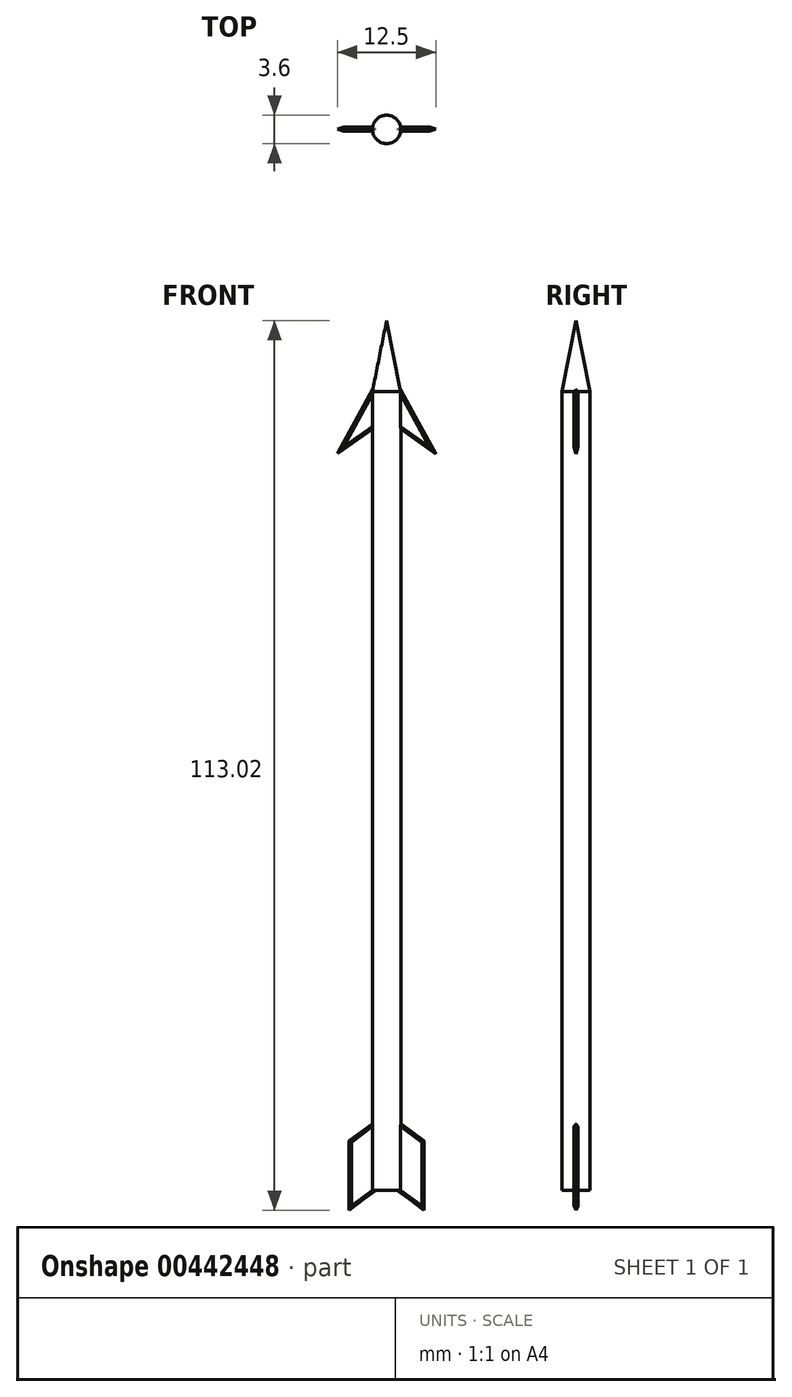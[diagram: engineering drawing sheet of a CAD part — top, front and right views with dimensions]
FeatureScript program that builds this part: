
annotation { "Feature Type Name" : "Feature", "Feature Type Description" : "" }
export const myFeature = defineFeature(function(context is Context, id is Id, definition is map)
    precondition{}
    {
        {
            var Q0;
            Q0=qCreatedBy(makeId("Front.planeOp"),FACE);
            var sketch = newSketch(context, id + "F0", { "sketchPlane" : qUnion([Q0])});
            skLineSegment(sketch, "E0", {"start": v(0, -61.4) * mm, "end": v(-1.8, -61.4) * mm});
            skLineSegment(sketch, "E1", {"start": v(-1.8, -61.4) * mm, "end": v(-1.8, 40.08) * mm});
            skLineSegment(sketch, "E2", {"start": v(-1.8, 40.08) * mm, "end": v(0, 40.08) * mm});
            skLineSegment(sketch, "E3", {"start": v(0, 40.08) * mm, "end": v(0, -61.4) * mm});
            skLineSegment(sketch, "E4", {"start": v(-1.8, 40.08) * mm, "end": v(0, 49.09) * mm});
            skLineSegment(sketch, "E5", {"start": v(0, 49.09) * mm, "end": v(0, 40.08) * mm});
            skSolve(sketch);
        }
        {
            var Q0;
            Q0=makeQuery(id+"F0.imprint","IMPRINT",FACE,{"disambiguationData":[TD([[makeQuery(id+"F0.imprint","IMPRINT",EDGE,{"derivedFrom":sQuery(id+"F0.wireOp",EDGE,"E0")}),-1.0]])]});
            var Q1;
            Q1=makeQuery(id+"F0.imprint","IMPRINT",FACE,{"disambiguationData":[TD([[makeQuery(id+"F0.imprint","IMPRINT",EDGE,{"derivedFrom":sQuery(id+"F0.wireOp",EDGE,"E2")}),1.0]])]});
            var Q2;
            Q2=sQuery(id+"F0.wireOp",EDGE,"E3");
            revolve(context, id + "F1", {"entities" : qUnion([Q0, Q1]), "axis" : qUnion([Q2]), "revolveType" : RevolveType.FULL});
        }
        {
            var Q0;
            Q0=qCreatedBy(makeId("Front.planeOp"),FACE);
            var sketch = newSketch(context, id + "F2", { "sketchPlane" : qUnion([Q0])});
            skLineSegment(sketch, "E6", {"start": v(0, 43.51) * mm, "end": v(-6.21, 32.2) * mm});
            skLineSegment(sketch, "E7", {"start": v(-6.21, 32.2) * mm, "end": v(0, 36.61) * mm});
            skLineSegment(sketch, "E8.MirrorCS", {"start": v(6.21, 32.2) * mm, "end": v(0, 36.61) * mm});
            skLineSegment(sketch, "E9.MirrorCS", {"start": v(0, 43.51) * mm, "end": v(6.21, 32.2) * mm});
            skSolve(sketch);
        }
        {
            var Q0;
            Q0=makeQuery(id+"F2.imprint","IMPRINT",FACE,{"disambiguationData":[TD([[makeQuery(id+"F2.imprint","IMPRINT",EDGE,{"derivedFrom":sQuery(id+"F2.wireOp",EDGE,"E6")}),1.0]])]});
            extrude(context, id + "F3", {"entities" : qUnion([Q0]), "operationType" : NewBodyOperationType.ADD, "depth" : 0.25 * mm});
        }
        {
            var Q0;
            Q0=qCreatedBy(makeId("Front.planeOp"),FACE);
            var sketch = newSketch(context, id + "F4", { "sketchPlane" : qUnion([Q0])});
            skLineSegment(sketch, "E10", {"start": v(6.25, 32.17) * mm, "end": v(0, 43.59) * mm});
            skLineSegment(sketch, "E11", {"start": v(0, 43.59) * mm, "end": v(-6.25, 32.2) * mm});
            skLineSegment(sketch, "E12", {"start": v(-6.25, 32.2) * mm, "end": v(0, 36.64) * mm});
            skLineSegment(sketch, "E13", {"start": v(0, 36.64) * mm, "end": v(6.25, 32.17) * mm});
            skSolve(sketch);
        }
        {
            var Q0;
            Q0=makeQuery(id+"F4.imprint","IMPRINT",FACE,{"disambiguationData":[TD([[makeQuery(id+"F4.imprint","IMPRINT",EDGE,{"derivedFrom":sQuery(id+"F4.wireOp",EDGE,"E10")}),1.0]])]});
            extrude(context, id + "F5", {"entities" : qUnion([Q0]), "operationType" : NewBodyOperationType.ADD, "oppositeDirection" : true, "depth" : 0.25 * mm});
        }
        {
            var Q0;
            Q0=makeQuery(id+"F5.opExtrude","CAP_EDGE",EDGE,{"disambiguationData":[OSD([sQuery(id+"F4.wireOp",EDGE,"E11")])],"isStart":false});
            var Q1;
            Q1=makeQuery(id+"F3.opExtrude","CAP_EDGE",EDGE,{"disambiguationData":[OSD([sQuery(id+"F2.wireOp",EDGE,"E6")])],"isStart":false});
            var Q2;
            Q2=makeQuery(id+"F3.opExtrude","CAP_EDGE",EDGE,{"disambiguationData":[OSD([sQuery(id+"F2.wireOp",EDGE,"E7")])],"isStart":false});
            var Q3;
            Q3=makeQuery(id+"F5.opExtrude","CAP_EDGE",EDGE,{"disambiguationData":[OSD([sQuery(id+"F4.wireOp",EDGE,"E12")])],"isStart":false});
            var Q4;
            Q4=makeQuery(id+"F3.opExtrude","CAP_EDGE",EDGE,{"disambiguationData":[OSD([sQuery(id+"F2.wireOp",EDGE,"E8.MirrorCS")])],"isStart":false});
            var Q5;
            Q5=makeQuery(id+"F5.opExtrude","CAP_EDGE",EDGE,{"disambiguationData":[OSD([sQuery(id+"F4.wireOp",EDGE,"E13")])],"isStart":false});
            var Q6;
            Q6=makeQuery(id+"F5.opExtrude","CAP_EDGE",EDGE,{"disambiguationData":[OSD([sQuery(id+"F4.wireOp",EDGE,"E10")])],"isStart":false});
            var Q7;
            Q7=makeQuery(id+"F3.opExtrude","CAP_EDGE",EDGE,{"disambiguationData":[OSD([sQuery(id+"F2.wireOp",EDGE,"E9.MirrorCS")])],"isStart":false});
            chamfer(context, id + "F6", {"entities" : qUnion([Q0, Q1, Q2, Q3, Q4, Q5, Q6, Q7]), "width" : 0.25 * mm, "tangentPropagation" : true});
        }
        {
            var Q0;
            Q0=qCreatedBy(makeId("Front.planeOp"),FACE);
            var sketch = newSketch(context, id + "F7", { "sketchPlane" : qUnion([Q0])});
            skLineSegment(sketch, "E14", {"start": v(0, -51.65) * mm, "end": v(-4.74, -55.14) * mm});
            skLineSegment(sketch, "E15", {"start": v(-4.74, -55.14) * mm, "end": v(-4.74, -63.89) * mm});
            skLineSegment(sketch, "E16", {"start": v(-4.74, -63.89) * mm, "end": v(0, -60.4) * mm});
            skLineSegment(sketch, "E17", {"start": v(0, -60.4) * mm, "end": v(0, -51.65) * mm});
            skLineSegment(sketch, "E18.MirrorCS", {"start": v(0, -51.65) * mm, "end": v(4.74, -55.14) * mm});
            skLineSegment(sketch, "E19.MirrorCS", {"start": v(4.74, -55.14) * mm, "end": v(4.74, -63.89) * mm});
            skLineSegment(sketch, "E20.MirrorCS", {"start": v(4.74, -63.89) * mm, "end": v(0, -60.4) * mm});
            skSolve(sketch);
        }
        {
            var Q0;
            Q0 = qSketchRegion(id + "F7", true);
            extrude(context, id + "F8", {"entities" : qUnion([Q0]), "operationType" : NewBodyOperationType.ADD, "depth" : 0.25 * mm});
        }
        {
            var Q0;
            Q0=qCreatedBy(makeId("Front.planeOp"),FACE);
            var sketch = newSketch(context, id + "F9", { "sketchPlane" : qUnion([Q0])});
            skLineSegment(sketch, "E21", {"start": v(0, -51.66) * mm, "end": v(4.78, -55.14) * mm});
            skLineSegment(sketch, "E22", {"start": v(4.78, -55.14) * mm, "end": v(4.78, -63.93) * mm});
            skLineSegment(sketch, "E23", {"start": v(4.78, -63.93) * mm, "end": v(0, -60.39) * mm});
            skLineSegment(sketch, "E24", {"start": v(0, -60.39) * mm, "end": v(0, -51.66) * mm});
            skLineSegment(sketch, "E25.MirrorCS", {"start": v(0, -51.66) * mm, "end": v(-4.78, -55.14) * mm});
            skLineSegment(sketch, "E26.MirrorCS", {"start": v(-4.78, -55.14) * mm, "end": v(-4.78, -63.93) * mm});
            skLineSegment(sketch, "E27.MirrorCS", {"start": v(-4.78, -63.93) * mm, "end": v(0, -60.39) * mm});
            skSolve(sketch);
        }
        {
            var Q0;
            Q0 = qSketchRegion(id + "F9", true);
            extrude(context, id + "F10", {"entities" : qUnion([Q0]), "operationType" : NewBodyOperationType.ADD, "oppositeDirection" : true, "depth" : 0.25 * mm});
        }
        {
            var Q0;
            Q0=makeQuery(id+"F10.opExtrude","CAP_EDGE",EDGE,{"disambiguationData":[OSD([sQuery(id+"F9.wireOp",EDGE,"E21")])],"isStart":false});
            var Q1;
            Q1=makeQuery(id+"F10.opExtrude","CAP_EDGE",EDGE,{"disambiguationData":[OSD([sQuery(id+"F9.wireOp",EDGE,"E22")])],"isStart":false});
            var Q2;
            Q2=makeQuery(id+"F10.opExtrude","CAP_EDGE",EDGE,{"disambiguationData":[OSD([sQuery(id+"F9.wireOp",EDGE,"E23")])],"isStart":false});
            var Q3;
            Q3=makeQuery(id+"F10.opExtrude","CAP_EDGE",EDGE,{"disambiguationData":[OSD([sQuery(id+"F9.wireOp",EDGE,"E27.MirrorCS")])],"isStart":false});
            var Q4;
            Q4=makeQuery(id+"F10.opExtrude","CAP_EDGE",EDGE,{"disambiguationData":[OSD([sQuery(id+"F9.wireOp",EDGE,"E26.MirrorCS")])],"isStart":false});
            var Q5;
            Q5=makeQuery(id+"F10.opExtrude","CAP_EDGE",EDGE,{"disambiguationData":[OSD([sQuery(id+"F9.wireOp",EDGE,"E25.MirrorCS")])],"isStart":false});
            var Q6;
            Q6=makeQuery(id+"F8.opExtrude","CAP_EDGE",EDGE,{"disambiguationData":[OSD([sQuery(id+"F7.wireOp",EDGE,"E14")])],"isStart":false});
            var Q7;
            Q7=makeQuery(id+"F8.opExtrude","CAP_EDGE",EDGE,{"disambiguationData":[OSD([sQuery(id+"F7.wireOp",EDGE,"E15")])],"isStart":false});
            var Q8;
            Q8=makeQuery(id+"F8.opExtrude","CAP_EDGE",EDGE,{"disambiguationData":[OSD([sQuery(id+"F7.wireOp",EDGE,"E16")])],"isStart":false});
            var Q9;
            Q9=makeQuery(id+"F8.opExtrude","CAP_EDGE",EDGE,{"disambiguationData":[OSD([sQuery(id+"F7.wireOp",EDGE,"E20.MirrorCS")])],"isStart":false});
            var Q10;
            Q10=makeQuery(id+"F8.opExtrude","CAP_EDGE",EDGE,{"disambiguationData":[OSD([sQuery(id+"F7.wireOp",EDGE,"E19.MirrorCS")])],"isStart":false});
            var Q11;
            Q11=makeQuery(id+"F8.opExtrude","CAP_EDGE",EDGE,{"disambiguationData":[OSD([sQuery(id+"F7.wireOp",EDGE,"E18.MirrorCS")])],"isStart":false});
            chamfer(context, id + "F11", {"entities" : qUnion([Q0, Q1, Q2, Q3, Q4, Q5, Q6, Q7, Q8, Q9, Q10, Q11]), "width" : 0.25 * mm, "tangentPropagation" : true});
        }
    });
